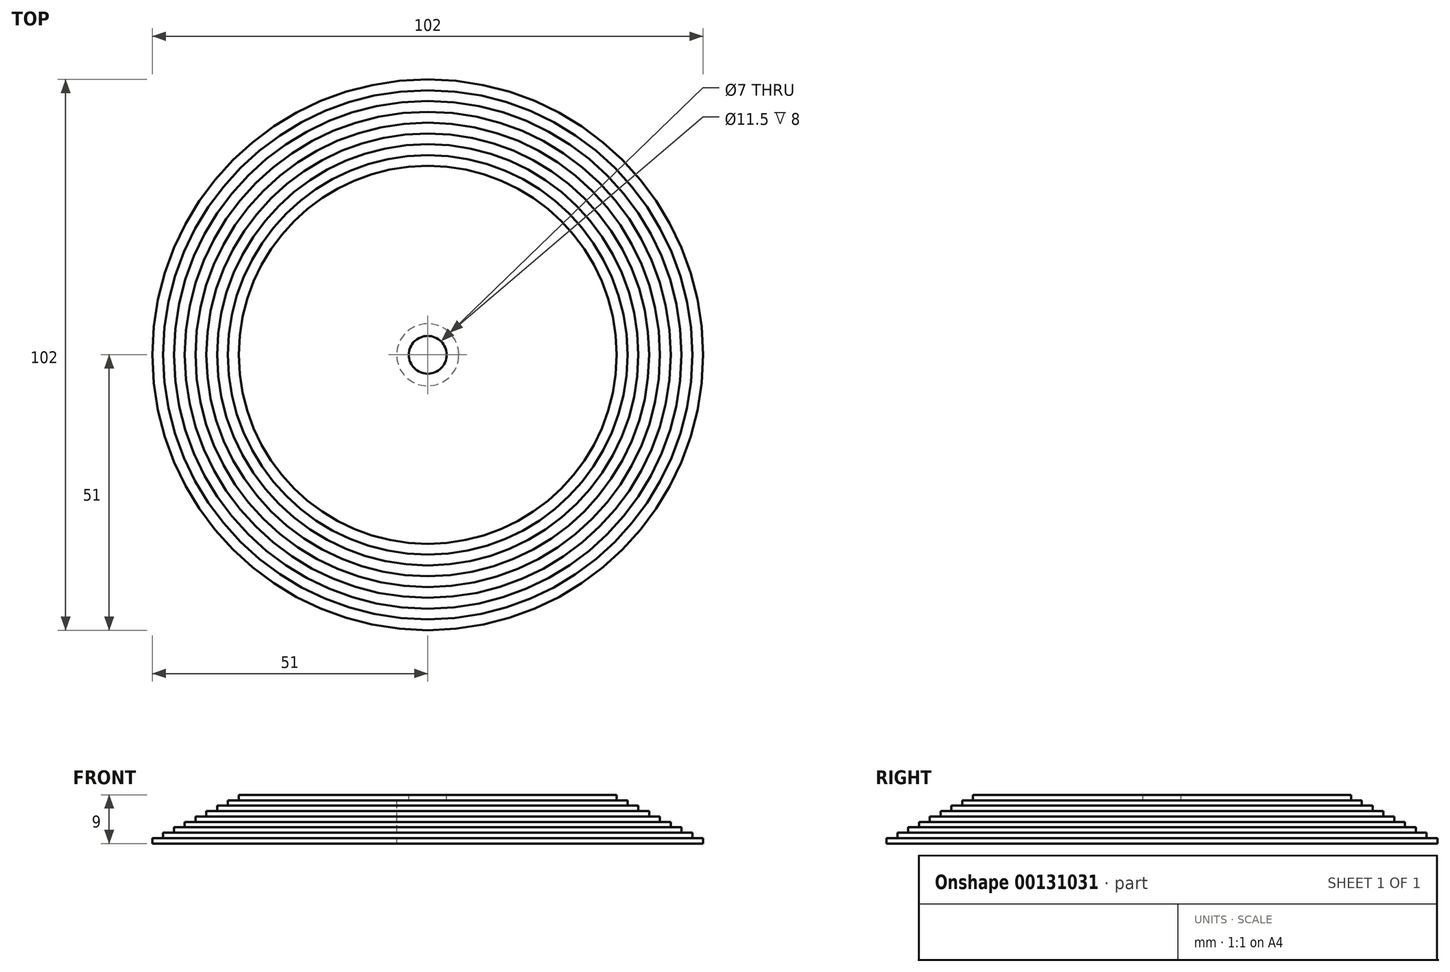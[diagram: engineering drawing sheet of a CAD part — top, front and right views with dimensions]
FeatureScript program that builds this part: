
annotation { "Feature Type Name" : "Feature", "Feature Type Description" : "" }
export const myFeature = defineFeature(function(context is Context, id is Id, definition is map)
    precondition{}
    {
        {
            var Q0;
            Q0=qCreatedBy(makeId("Front.planeOp"),FACE);
            var sketch = newSketch(context, id + "F0", { "sketchPlane" : qUnion([Q0])});
            skLineSegment(sketch, "E0", {"start": v(0, 0) * mm, "end": v(0, 9) * mm});
            skLineSegment(sketch, "E1", {"start": v(0, 9) * mm, "end": v(35, 9) * mm});
            skLineSegment(sketch, "E2", {"start": v(35, 9) * mm, "end": v(35, 8) * mm});
            skLineSegment(sketch, "E3", {"start": v(35, 8) * mm, "end": v(37, 8) * mm});
            skLineSegment(sketch, "E4", {"start": v(37, 8) * mm, "end": v(37, 7) * mm});
            skLineSegment(sketch, "E5", {"start": v(37, 7) * mm, "end": v(39, 7) * mm});
            skLineSegment(sketch, "E6", {"start": v(39, 7) * mm, "end": v(39, 6) * mm});
            skLineSegment(sketch, "E7", {"start": v(39, 6) * mm, "end": v(41, 6) * mm});
            skLineSegment(sketch, "E8", {"start": v(41, 6) * mm, "end": v(41, 5) * mm});
            skLineSegment(sketch, "E9", {"start": v(41, 5) * mm, "end": v(43, 5) * mm});
            skLineSegment(sketch, "E10", {"start": v(43, 5) * mm, "end": v(43, 4) * mm});
            skLineSegment(sketch, "E11", {"start": v(43, 4) * mm, "end": v(45, 4) * mm});
            skLineSegment(sketch, "E12", {"start": v(45, 4) * mm, "end": v(45, 3) * mm});
            skLineSegment(sketch, "E13", {"start": v(45, 3) * mm, "end": v(47, 3) * mm});
            skLineSegment(sketch, "E14", {"start": v(47, 3) * mm, "end": v(47, 2) * mm});
            skLineSegment(sketch, "E15", {"start": v(47, 2) * mm, "end": v(49, 2) * mm});
            skLineSegment(sketch, "E16", {"start": v(49, 2) * mm, "end": v(49, 1) * mm});
            skLineSegment(sketch, "E17", {"start": v(49, 1) * mm, "end": v(51, 1) * mm});
            skLineSegment(sketch, "E18", {"start": v(51, 1) * mm, "end": v(51, 0) * mm});
            skLineSegment(sketch, "E19", {"start": v(51, 0) * mm, "end": v(0, 0) * mm});
            skSolve(sketch);
        }
        {
            var Q0;
            Q0=makeQuery(id+"F0.imprint","IMPRINT",FACE,{"disambiguationData":[TD([[makeQuery(id+"F0.imprint","IMPRINT",EDGE,{"derivedFrom":sQuery(id+"F0.wireOp",EDGE,"E0")}),-1.0]])]});
            var Q1;
            Q1=sQuery(id+"F0.wireOp",EDGE,"E0");
            revolve(context, id + "F1", {"entities" : qUnion([Q0]), "axis" : qUnion([Q1]), "revolveType" : RevolveType.FULL});
        }
        {
            var Q0;
            Q0=makeQuery(id+"F1.opRevolve","SWEPT_FACE",FACE,{"disambiguationData":[OSD([sQuery(id+"F0.wireOp",EDGE,"E1")])]});
            var sketch = newSketch(context, id + "F2", { "sketchPlane" : qUnion([Q0])});
            skCircle(sketch, "E20", {"center": v(0, 0) * mm, "radius": 3.5 * mm});
            skSolve(sketch);
        }
        {
            var Q0;
            Q0 = qSketchRegion(id + "F2", true);
            extrude(context, id + "F3", {"entities" : qUnion([Q0]), "operationType" : NewBodyOperationType.REMOVE, "endBound" : BoundingType.THROUGH_ALL, "oppositeDirection" : true, "depth" : 25 * mm});
        }
        {
            var Q0;
            Q0=makeQuery(id+"F1.opRevolve","SWEPT_FACE",FACE,{"disambiguationData":[OSD([sQuery(id+"F0.wireOp",EDGE,"E19")])]});
            var sketch = newSketch(context, id + "F4", { "sketchPlane" : qUnion([Q0])});
            skCircle(sketch, "E21", {"center": v(0, 0) * mm, "radius": 5.75 * mm});
            skSolve(sketch);
        }
        {
            var Q0;
            Q0 = qSketchRegion(id + "F4", true);
            extrude(context, id + "F5", {"entities" : qUnion([Q0]), "operationType" : NewBodyOperationType.REMOVE, "oppositeDirection" : true, "depth" : 8 * mm});
        }
    });
